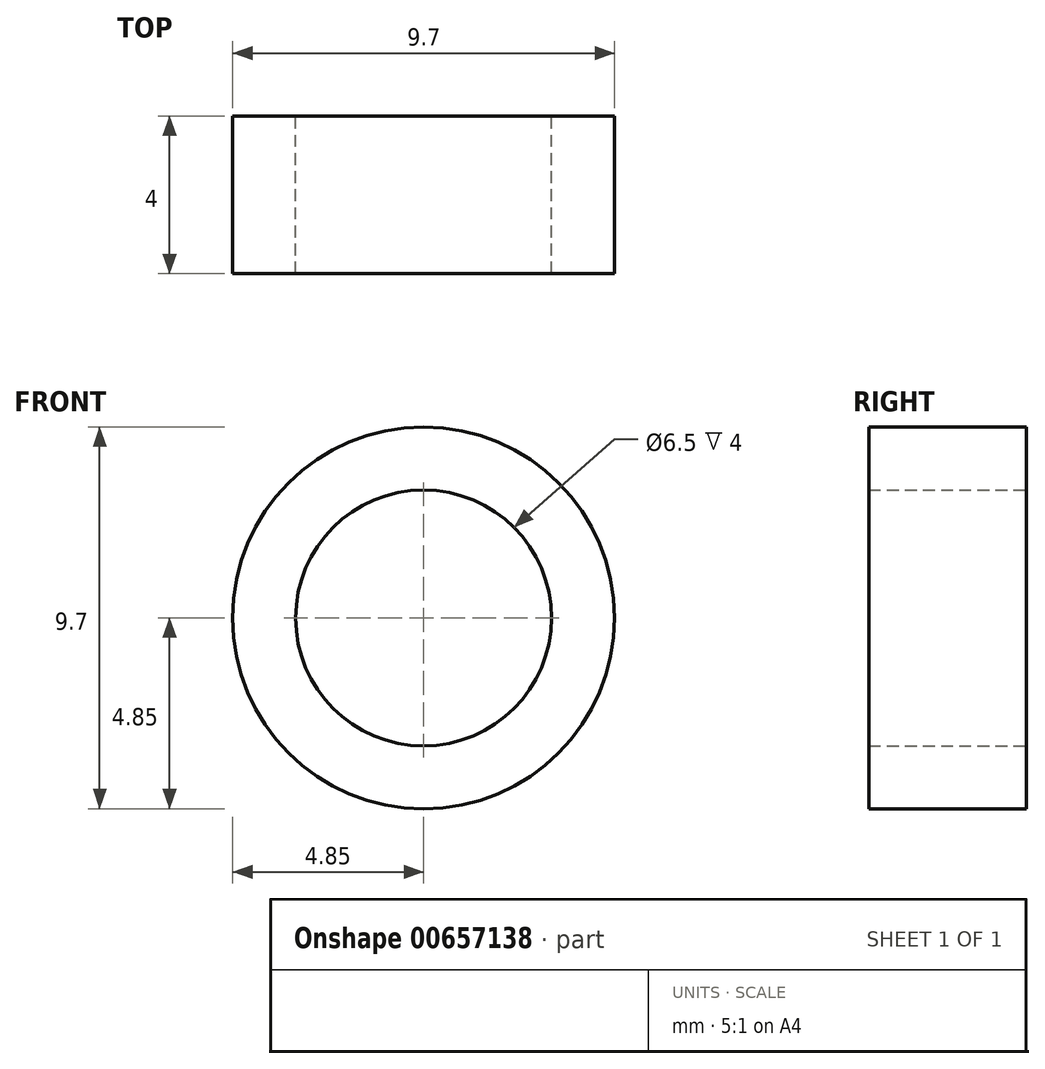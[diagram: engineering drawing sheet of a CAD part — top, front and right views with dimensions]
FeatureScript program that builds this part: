
annotation { "Feature Type Name" : "Feature", "Feature Type Description" : "" }
export const myFeature = defineFeature(function(context is Context, id is Id, definition is map)
    precondition{}
    {
        {
            var Q0;
            Q0=qCreatedBy(makeId("Front.planeOp"),FACE);
            var sketch = newSketch(context, id + "F0", { "sketchPlane" : qUnion([Q0])});
            skCircle(sketch, "E0", {"center": v(0, 0) * mm, "radius": 3.25 * mm});
            skCircle(sketch, "E1", {"center": v(0, 0) * mm, "radius": 4.85 * mm});
            skSolve(sketch);
        }
        {
            var Q0;
            Q0 = qSketchRegion(id + "F0", true);
            extrude(context, id + "F1", {"entities" : qUnion([Q0]), "depth" : 4 * mm, "offsetDistance" : 25 * mm});
        }
    });
